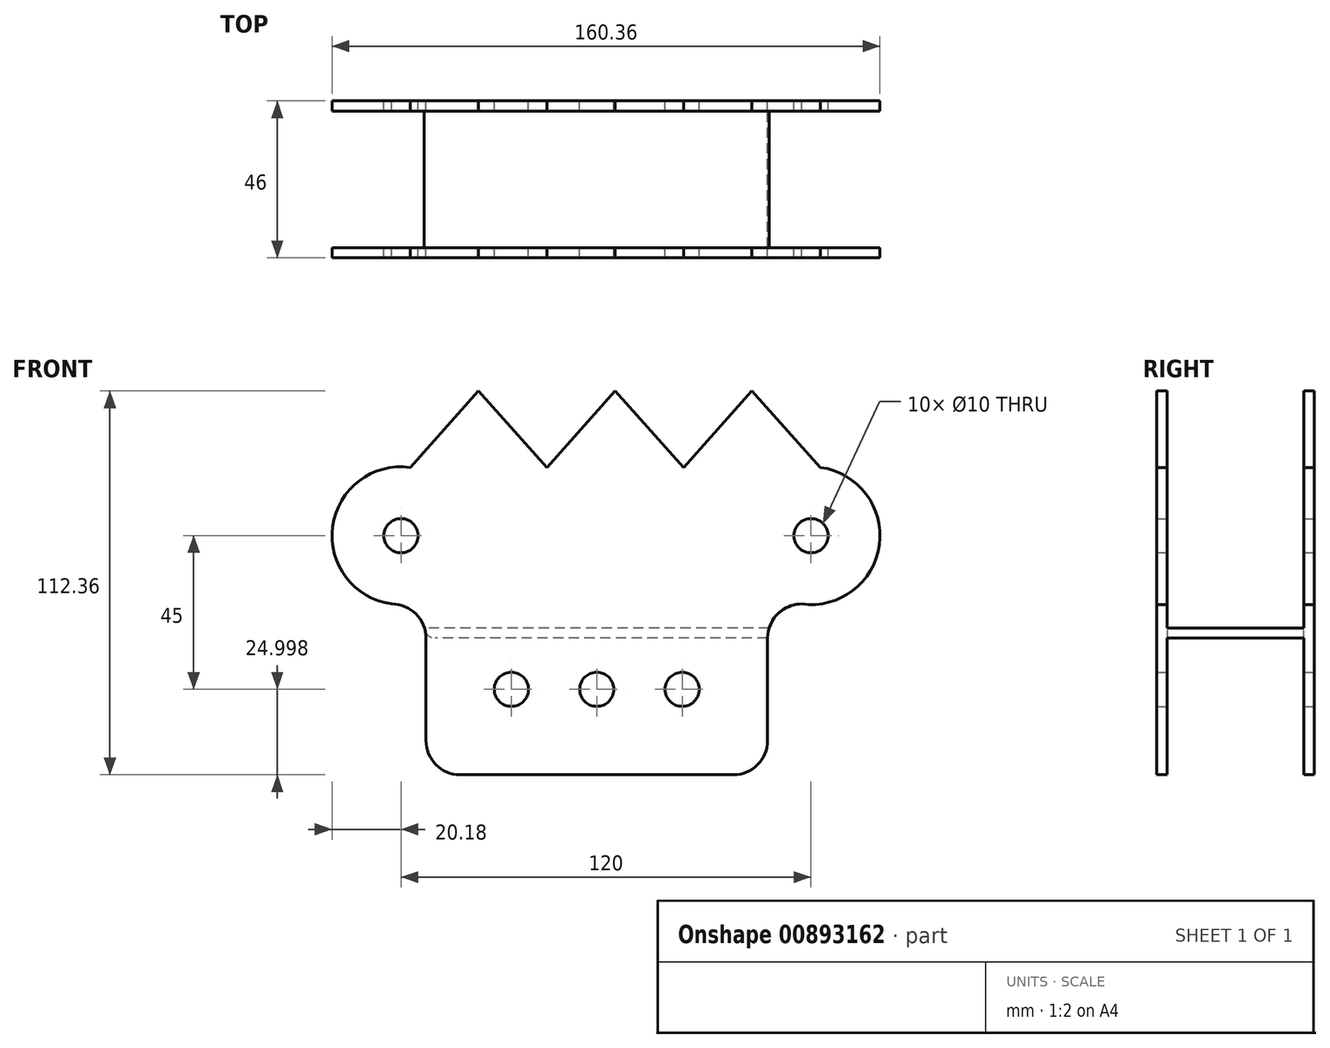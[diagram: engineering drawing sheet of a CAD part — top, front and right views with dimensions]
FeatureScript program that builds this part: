
annotation { "Feature Type Name" : "Feature", "Feature Type Description" : "" }
export const myFeature = defineFeature(function(context is Context, id is Id, definition is map)
    precondition{}
    {
        {
            var Q0;
            Q0=qCreatedBy(makeId("Front.planeOp"),FACE);
            var sketch = newSketch(context, id + "F0", { "sketchPlane" : qUnion([Q0])});
            skPoint(sketch, "E0.start.orphan", {"position": v(-74.6, -4.3) * mm});
            skPoint(sketch, "E1.orphan", {"position": v(-74.6, 15.7) * mm});
            skPoint(sketch, "E2.orphan", {"position": v(-74.6, -24.3) * mm});
            skLineSegment(sketch, "E3", {"start": v(-54.6, 15.7) * mm, "end": v(-34.6, 38.07) * mm});
            skLineSegment(sketch, "E4", {"start": v(-34.6, 38.07) * mm, "end": v(-14.6, 15.7) * mm});
            skLineSegment(sketch, "E5", {"start": v(-14.6, 15.7) * mm, "end": v(5.4, 38.07) * mm});
            skLineSegment(sketch, "E6", {"start": v(5.4, 38.07) * mm, "end": v(25.4, 15.7) * mm});
            skLineSegment(sketch, "E7", {"start": v(25.4, 15.7) * mm, "end": v(45.4, 38.07) * mm});
            skLineSegment(sketch, "E8", {"start": v(45.4, 38.07) * mm, "end": v(65.4, 15.7) * mm});
            skPoint(sketch, "E9.end.orphan", {"position": v(5.4, 15.7) * mm});
            skPoint(sketch, "E10.end.orphan", {"position": v(-34.6, 15.7) * mm});
            skPoint(sketch, "E11.start.orphan", {"position": v(85.4, 38.07) * mm});
            skArc(sketch, "E12", {"start": v(60, -24.3) * mm, "mid": v(82.7, -7) * mm, "end": v(65.4, 15.7) * mm});
            skArc(sketch, "E13", {"start": v(-54.6, 15.7) * mm, "mid": v(-77.3, -1.6) * mm, "end": v(-60, -24.3) * mm});
            skCircle(sketch, "E14", {"center": v(-57.3, -4.3) * mm, "radius": 5 * mm});
            skCircle(sketch, "E15", {"center": v(62.7, -4.3) * mm, "radius": 5 * mm});
            skLineSegment(sketch, "E16", {"start": v(60, -24.3) * mm, "end": v(60, -24.3) * mm});
            skLineSegment(sketch, "E17", {"start": v(50, -34.3) * mm, "end": v(50, -64.3) * mm});
            skLineSegment(sketch, "E18", {"start": v(40, -74.3) * mm, "end": v(-40, -74.3) * mm});
            skLineSegment(sketch, "E19", {"start": v(-60, -24.3) * mm, "end": v(-60, -24.3) * mm});
            skLineSegment(sketch, "E20", {"start": v(-50, -34.3) * mm, "end": v(-50, -64.3) * mm});
            skPoint(sketch, "E21.start.orphan", {"position": v(50, -49.3) * mm});
            skCircle(sketch, "E22", {"center": v(0, -49.3) * mm, "radius": 5 * mm});
            skCircle(sketch, "E23", {"center": v(-25, -49.3) * mm, "radius": 5 * mm});
            skCircle(sketch, "E24", {"center": v(25, -49.3) * mm, "radius": 5 * mm});
            skPoint(sketch, "E25.visualSharp", {"position": v(-50, -24.3) * mm});
            skArc(sketch, "E25.filletArc", {"start": v(-50, -34.3) * mm, "mid": v(-52.93, -27.22) * mm, "end": v(-60, -24.3) * mm});
            skPoint(sketch, "E26.visualSharp", {"position": v(50, -24.3) * mm});
            skArc(sketch, "E26.filletArc", {"start": v(60, -24.3) * mm, "mid": v(52.93, -27.22) * mm, "end": v(50, -34.3) * mm});
            skPoint(sketch, "E27.visualSharp", {"position": v(50, -74.3) * mm});
            skArc(sketch, "E27.filletArc", {"start": v(40, -74.3) * mm, "mid": v(47.07, -71.36) * mm, "end": v(50, -64.3) * mm});
            skPoint(sketch, "E28.visualSharp", {"position": v(-50, -74.3) * mm});
            skArc(sketch, "E28.filletArc", {"start": v(-50, -64.3) * mm, "mid": v(-47.07, -71.36) * mm, "end": v(-40, -74.3) * mm});
            skSolve(sketch);
        }
        {
            var Q0;
            Q0 = qSketchRegion(id + "F0", true);
            extrude(context, id + "F1", {"entities" : qUnion([Q0]), "depth" : 46 * mm, "offsetDistance" : 25 * mm});
        }
        {
            var Q0;
            Q0=makeQuery(id+"F1.opExtrude","SWEPT_FACE",FACE,{"disambiguationData":[OSD([sQuery(id+"F0.wireOp",EDGE,"E20")])]});
            var sketch = newSketch(context, id + "F2", { "sketchPlane" : qUnion([Q0])});
            skLineSegment(sketch, "E29", {"start": v(3, -34.3) * mm, "end": v(43, -34.3) * mm});
            skLineSegment(sketch, "E30", {"start": v(43, -34.3) * mm, "end": v(43, -96.73) * mm});
            skLineSegment(sketch, "E31", {"start": v(43, -96.73) * mm, "end": v(3, -96.73) * mm});
            skLineSegment(sketch, "E32", {"start": v(3, -96.73) * mm, "end": v(3, 77.4) * mm});
            skLineSegment(sketch, "E33", {"start": v(3, 77.4) * mm, "end": v(43, 77.4) * mm});
            skLineSegment(sketch, "E34", {"start": v(43, 77.4) * mm, "end": v(43, -31.3) * mm});
            skLineSegment(sketch, "E35", {"start": v(3, -31.3) * mm, "end": v(43, -31.3) * mm});
            skSolve(sketch);
        }
        {
            var Q0;
            Q0 = qSketchRegion(id + "F2", true);
            extrude(context, id + "F3", {"entities" : qUnion([Q0]), "operationType" : NewBodyOperationType.REMOVE, "endBound" : BoundingType.THROUGH_ALL, "oppositeDirection" : true, "depth" : 25 * mm, "offsetDistance" : 25 * mm});
        }
        {
            var Q0;
            Q0 = qSketchRegion(id + "F2", true);
            extrude(context, id + "F4", {"entities" : qUnion([Q0]), "operationType" : NewBodyOperationType.REMOVE, "endBound" : BoundingType.THROUGH_ALL, "depth" : 25 * mm, "offsetDistance" : 25 * mm});
        }
        {
            var Q0;
            Q0=makeQuery(id+"F3.boolean.opBoolean","MERGE",EDGE,{"derivedFrom":[makeQuery(id+"F1.opExtrude","SWEPT_EDGE",EDGE,{"disambiguationData":[OSD([sQuery(id+"F0.wireOp",EDGE,"E20"),sQuery(id+"F0.wireOp",EDGE,"E25.filletArc")])]})],"fromTools":[makeQuery(id+"F3.opExtrude","CAP_EDGE",EDGE,{"disambiguationData":[OSD([sQuery(id+"F2.wireOp",EDGE,"E29")])],"isStart":true})]});
            var Q1;
            {var subQ0=sQuery(id+"F0.wireOp",EDGE,"E26.filletArc");Q1=makeQuery(id+"F3.boolean.opBoolean","SPLIT",EDGE,{"disambiguationData":[topologyDisambiguationEdgeConnected([makeQuery(id+"F1.opExtrude","SWEPT_FACE",FACE,{"disambiguationData":[OSD([subQ0])]}),makeQuery(id+"F3.opExtrude","SWEPT_FACE",FACE,{"disambiguationData":[OSD([sQuery(id+"F2.wireOp",EDGE,"E29")])]})])],"derivedFrom":makeQuery(id+"F1.opExtrude","SWEPT_EDGE",EDGE,{"disambiguationData":[OSD([sQuery(id+"F0.wireOp",EDGE,"E17"),subQ0])]})});}
            fillet(context, id + "F5", {"entities" : qUnion([Q0, Q1]), "tangentPropagation" : true, "radius" : 3 * mm, "defaultsChanged" : false, "vertexSettings" : [], "allowEdgeOverflow" : false});
        }
    });
